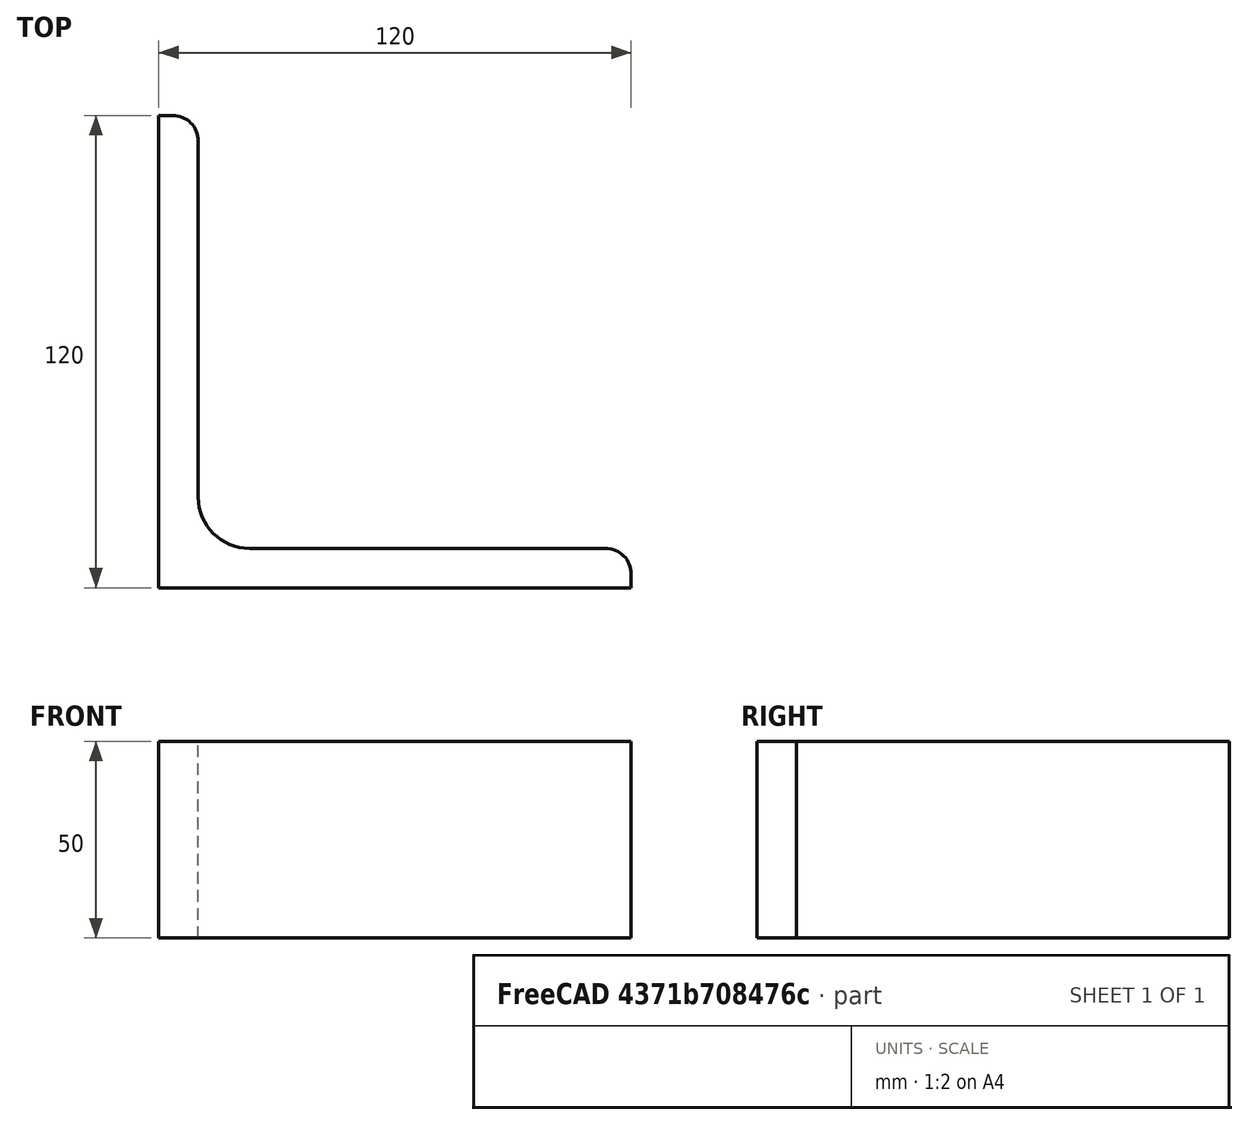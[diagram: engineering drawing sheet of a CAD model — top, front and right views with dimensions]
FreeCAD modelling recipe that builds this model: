
FCSTD DOCUMENT  (FreeCAD 0.15R4671 (Git))
Label: Angle Bar L120x120x10 EN10056 S235JR
License: All rights reserved
LicenseURL: http://en.wikipedia.org/wiki/All_rights_reserved
objects: Sketcher::SketchObject×1, Part::Extrusion×1
note: 2 computed .brp shape members not serialized (recipe doc carries the construction recipe); baked Part::Feature solids carry a one-line shape summary decoded from their .brp

FEATURE [Sketcher::SketchObject] Sketch
  sketch-geometry (9):
    g0: LineSegment StartX=0 StartY=0 StartZ=0 EndX=120 EndY=0 EndZ=0
    g1: LineSegment StartX=120 StartY=0 StartZ=0 EndX=120 EndY=3.5 EndZ=0
    g2: LineSegment StartX=113.5 StartY=10 StartZ=0 EndX=23 EndY=10 EndZ=0
    g3: LineSegment StartX=0 StartY=0 StartZ=0 EndX=0 EndY=120 EndZ=0
    g4: LineSegment StartX=0 StartY=120 StartZ=0 EndX=3.5 EndY=120 EndZ=0
    g5: LineSegment StartX=10 StartY=113.5 StartZ=0 EndX=10 EndY=23 EndZ=0
    g6: ArcOfCircle CenterX=23 CenterY=23 CenterZ=0 NormalX=0 NormalY=0 NormalZ=1 Radius=13 StartAngle=3.14159 EndAngle=4.71239
    g7: ArcOfCircle CenterX=3.5 CenterY=113.5 CenterZ=0 NormalX=0 NormalY=0 NormalZ=1 Radius=6.5 StartAngle=0 EndAngle=1.5708
    g8: ArcOfCircle CenterX=113.5 CenterY=3.5 CenterZ=0 NormalX=0 NormalY=0 NormalZ=1 Radius=6.5 StartAngle=0 EndAngle=1.5708
  constraints (23):
    c: Coincident(g0,g-1)
    c: Horizontal(g0)
    c: Coincident(g1,g0)
    c: Vertical(g1)
    c: Horizontal(g2)
    c: Coincident(g3,g-1)
    c: Vertical(g3)
    c: Coincident(g4,g3)
    c: Horizontal(g4)
    c: Vertical(g5)
    c: Tangent(g5,g6) = -1.5708
    c: Tangent(g2,g6) = 1.5708
    c: Tangent(g4,g7) = 1.5708
    c: Tangent(g5,g7) = 1.5708
    c: Tangent(g2,g8) = -1.5708
    c: Tangent(g1,g8) = -1.5708
    c: DistanceX(g0) = 120
    c: DistanceY(g3) = 120
    c: DistanceY(g0,g2) = 10
    c: DistanceX(g3,g5) = 10
    c: Radius(g6) = 13
    c: Radius(g8) = 6.5
    c: Radius(g7) = 6.5
FEATURE [Part::Extrusion] Extrude  label="Angle Bar L120x120x10 EN10056 S235JR"
  Base = -> Sketch
  Dir = (0,0,50)
  Solid = true
